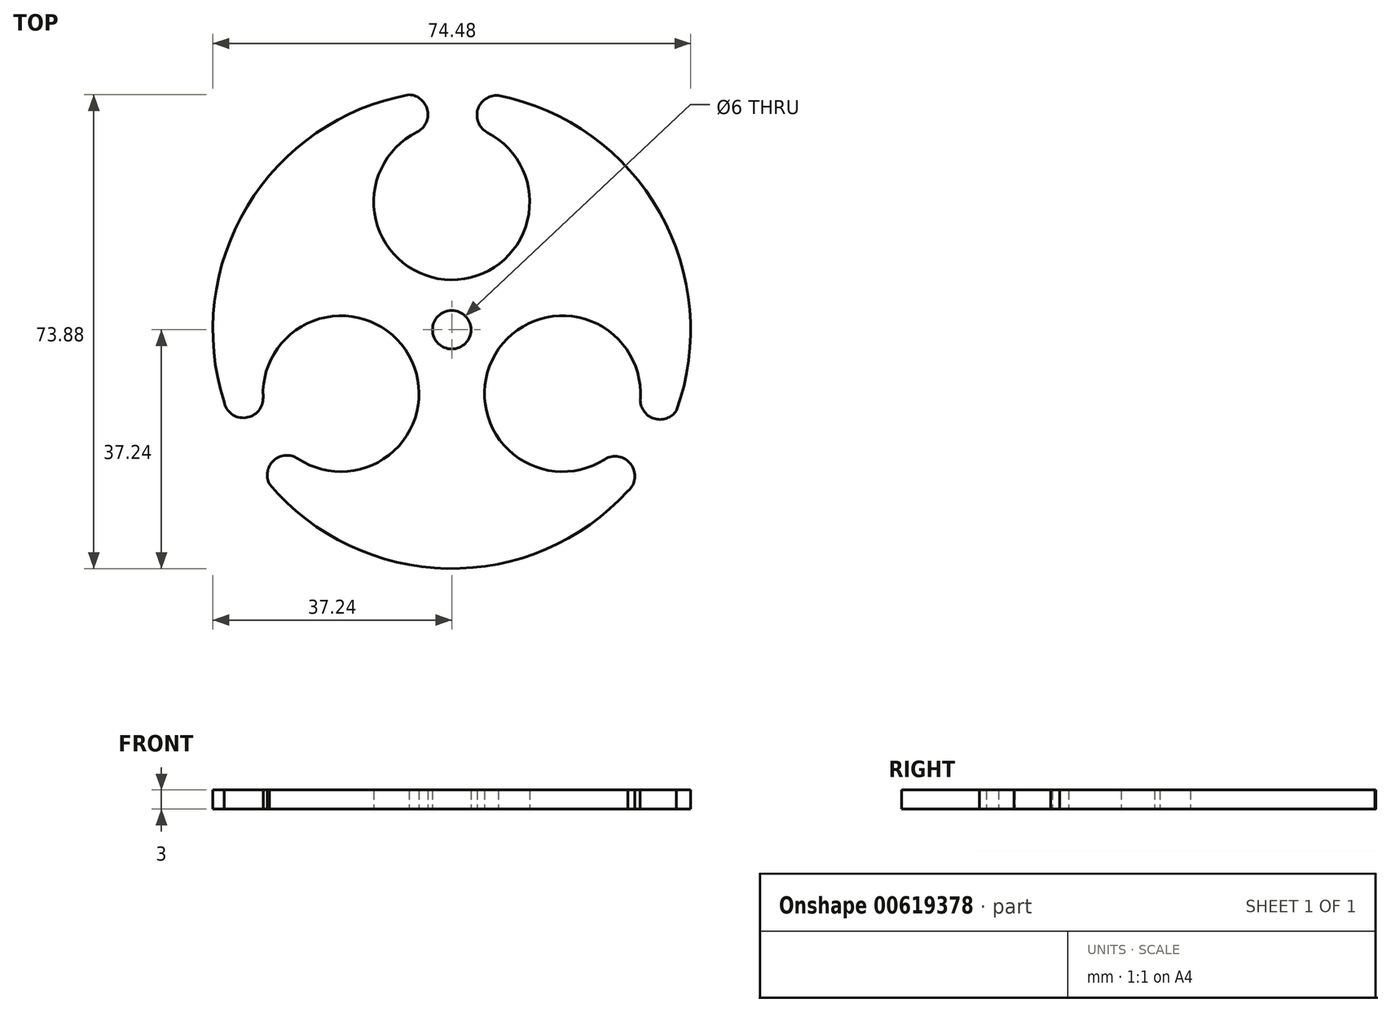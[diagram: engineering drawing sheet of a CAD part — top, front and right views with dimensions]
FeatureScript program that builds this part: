
annotation { "Feature Type Name" : "Feature", "Feature Type Description" : "" }
export const myFeature = defineFeature(function(context is Context, id is Id, definition is map)
    precondition{}
    {
        {
            var Q0;
            Q0=qCreatedBy(makeId("Top.planeOp"),FACE);
            var sketch = newSketch(context, id + "F0", { "sketchPlane" : qUnion([Q0])});
            skLineSegment(sketch, "E0.bottom", {"start": v(0, 0) * mm, "end": v(75, 0) * mm, "construction": true});
            skLineSegment(sketch, "E0.top", {"start": v(0, 75) * mm, "end": v(75, 75) * mm, "construction": true});
            skLineSegment(sketch, "E0.left", {"start": v(0, 0) * mm, "end": v(0, 75) * mm, "construction": true});
            skLineSegment(sketch, "E0.right", {"start": v(75, 0) * mm, "end": v(75, 75) * mm, "construction": true});
            skLineSegment(sketch, "E1", {"start": v(0, 75) * mm, "end": v(75, 0) * mm, "construction": true});
            skArc(sketch, "E2", {"start": v(30.88, 74.14) * mm, "mid": v(5.42, 56.4) * mm, "end": v(2.24, 25.52) * mm});
            skCircle(sketch, "E3", {"center": v(37.5, 37.5) * mm, "radius": 3 * mm});
            skArc(sketch, "E4", {"start": v(32.09, 68.31) * mm, "mid": v(37.4, 45.28) * mm, "end": v(43.1, 68.22) * mm});
            skArc(sketch, "E5", {"start": v(32.09, 68.31) * mm, "mid": v(33.73, 71.7) * mm, "end": v(30.88, 74.14) * mm});
            skArc(sketch, "E6", {"start": v(45.52, 73.86) * mm, "mid": v(41.69, 72.17) * mm, "end": v(43.1, 68.22) * mm});
            skArc(sketch, "E7.1.0", {"start": v(13.52, 17.4) * mm, "mid": v(30.81, 33.52) * mm, "end": v(8.1, 26.98) * mm});
            skArc(sketch, "E7.1.1", {"start": v(13.52, 17.4) * mm, "mid": v(9.77, 17.14) * mm, "end": v(9.08, 13.45) * mm});
            skArc(sketch, "E7.1.2", {"start": v(2, 26.27) * mm, "mid": v(5.38, 23.8) * mm, "end": v(8.1, 26.98) * mm});
            skArc(sketch, "E7.2.0", {"start": v(66.9, 26.78) * mm, "mid": v(44.3, 33.7) * mm, "end": v(61.3, 17.3) * mm});
            skArc(sketch, "E7.2.1", {"start": v(66.9, 26.78) * mm, "mid": v(69, 23.67) * mm, "end": v(72.54, 24.91) * mm});
            skArc(sketch, "E7.2.2", {"start": v(64.98, 12.37) * mm, "mid": v(65.43, 16.54) * mm, "end": v(61.3, 17.3) * mm});
            skArc(sketch, "E8.trimOffspring", {"start": v(72.54, 24.91) * mm, "mid": v(69.9, 55.84) * mm, "end": v(44.75, 74.02) * mm});
            skArc(sketch, "E9.trimOffspring", {"start": v(9.08, 13.45) * mm, "mid": v(37.18, 0.27) * mm, "end": v(65.5, 12.96) * mm});
            skSolve(sketch);
        }
        {
            var Q0;
            {var subQ0=sQuery(id+"F0.wireOp",EDGE,"E7.1.2");var subQ1=sQuery(id+"F0.wireOp",EDGE,"E2");var subQ2=makeQuery(id+"F0.imprint","INTERSECT",VERTEX,{"disambiguationData":[OD(0.0)],"derivedFrom":[subQ1,subQ0]});Q0=makeQuery(id+"F0.imprint","IMPRINT",FACE,{"disambiguationData":[TD([[makeQuery(id+"F0.imprint","IMPRINT",EDGE,{"disambiguationData":[TD([[subQ2,1.0]])],"derivedFrom":subQ1}),-1.0]])]});}
            var Q1;
            {var subQ0=sQuery(id+"F0.wireOp",EDGE,"E8.trimOffspring");var subQ1=sQuery(id+"F0.wireOp",EDGE,"E6");var subQ2=makeQuery(id+"F0.imprint","INTERSECT",VERTEX,{"disambiguationData":[OD(0.0)],"derivedFrom":[subQ1,subQ0]});Q1=makeQuery(id+"F0.imprint","IMPRINT",FACE,{"disambiguationData":[TD([[makeQuery(id+"F0.imprint","IMPRINT",EDGE,{"disambiguationData":[TD([[subQ2,-1.0]])],"derivedFrom":subQ1}),1.0]])]});}
            var Q2;
            {var subQ0=sQuery(id+"F0.wireOp",EDGE,"E9.trimOffspring");var subQ1=sQuery(id+"F0.wireOp",EDGE,"E7.2.2");var subQ2=makeQuery(id+"F0.imprint","INTERSECT",VERTEX,{"disambiguationData":[OD(0.0)],"derivedFrom":[subQ1,subQ0]});Q2=makeQuery(id+"F0.imprint","IMPRINT",FACE,{"disambiguationData":[TD([[makeQuery(id+"F0.imprint","IMPRINT",EDGE,{"disambiguationData":[TD([[subQ2,-1.0]])],"derivedFrom":subQ1}),1.0]])]});}
            var Q3;
            Q3=makeQuery(id+"F0.imprint","IMPRINT",FACE,{"disambiguationData":[TD([[makeQuery(id+"F0.imprint","IMPRINT",EDGE,{"derivedFrom":sQuery(id+"F0.wireOp",EDGE,"E3")}),-1.0]])]});
            extrude(context, id + "F1", {"entities" : qUnion([Q0, Q1, Q2, Q3]), "depth" : 3 * mm, "offsetDistance" : 25 * mm});
        }
    });
